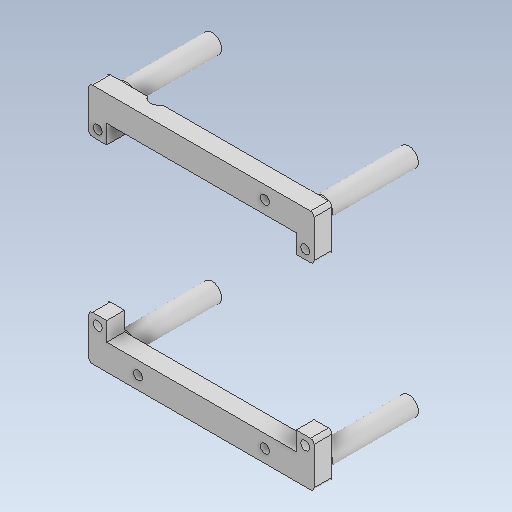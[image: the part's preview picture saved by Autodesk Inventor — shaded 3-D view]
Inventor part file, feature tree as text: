
AUTODESK INVENTOR PART (.ipt)
format: ipt  version: 2021.3 (Build 253353010, 353A)  size: 272,896 bytes
history: native  units: mm
features: sketch x4, reference x4, projected_geometry x4, extrude x3, other x3, fillet x2, hole x1, plane x1
ambient origin geometry x8: Origin, YZ Plane, XZ Plane, XY Plane, X Axis, Y Axis, Z Axis, Center Point
bodies: Volumenkörper1 (feature_tree)
feature tree (22):
  extrude  "fuss"  Depth=10.0mm TaperAngle=0.0deg
  extrude  "Saeulen"  Depth=4.0mm
  hole  "Bohrung1"  [1 undecoded]
  fillet  "Rundung1"  Radius=5.0mm
  fillet  "Rundung2"  Radius=3.0mm
  sketch  "Skizze4"  dims[d11=6.0mm d12=8.5mm d13=2.0mm d14=90.0deg d15=8.0mm d16=20.594885mm d17=3.0mm d18=2.0mm d19=12.5mm d20=16.5mm d21=55.0mm d22=0.0mm d23=10.0mm d24=0.5mm d25=0.5mm d26=0.5mm d27=0.5mm d28=0.5mm d29=10.0mm d31=0.5mm]
  plane  "Arbeitsebene1"
  extrude  "aussparung_strom"  Depth=2.0mm
  sketch  "Skizze1"  dims[d0=15.0mm d2=10.0mm d3=0.0mm]
  reference  "Referenz1"
  reference  "Referenz2"
  sketch  "Skizze2"  dims[d4=10.6mm d5=4.0mm]
  projected_geometry  "Projizierte Kontur1"
  projected_geometry  "Projizierte Kontur2"
  sketch  "Skizze3"  dims[d6=51.0mm d7=0.0mm d9=19.5mm d10=5.0mm]
  projected_geometry  "Projizierte Kontur3"
  projected_geometry  "Projizierte Kontur4"
  reference  "Referenz3"
  reference  "Referenz4"
  other  "<userpath>\Documents\Inventor\Scoomatic-Jetson\scoomatic_halterung_bg.iam"
  other  "scoomatic_halterung_bg.iam"
  other  "jetson_dummy:1"
note: 1 required parameter value undecoded (feature->parameter linkage not recoverable at this tier; creation-order binding heuristic only, values carry confidence <= 0.55)
